# Revit family: ONRIZH
name_source: partatom
category: Mechanical Equipment
units: mm (PartAtom-declared; Revit-internal decimal feet)

## family parameters
Always vertical = Yes
Cut with Voids When Loaded = No
OmniClass Number = 23.40.40.11.17
OmniClass Title = Refrigerated Cases
Part Type = Normal
Room Calculation Point = No
Round Connector Dimension = Use Radius
Shared = No
Work Plane-Based = Yes

## types (5) — shared parameters
22" Shelf = Yes
Certifications = NSF 7, UL471, CSA
DATE = 02/08/2016
DISCHARGE AIR TEMP. = -8 °F
DISCHARGE AIR VELOCITY = 350 FPM
Default Elevation = 48"
Defrost Num Day = 4
Defrost Termination = 50 °F
Defrost Type = ELECTRIC DEFROST
Defrosts Per Day_2 = 1
Description = High Narrow Back-to-Back Reach-In Glass Door Merchandiser
Discharge Air (F) = -1
Discharge Air Velocity (FPM) = 350 FPM
Door Type = Heated
EQUIPMENT DESCRIPTION = High Narrow Back-to-Back Reach-In Glass Door Merchandiser
EQUIPMENT MARK = ONRIZH
Electric Defrost Fail-Safe = 46
Electric Defrost Run-Off Time (Min) = 0
Electric Defrost Termination = 50
Evap Temp = -15
Height = 85 1/4"
Hot Gas Defrost Fail-Safe = 24
Hot Gas Defrost Run-Off Time (Min) = 13-15
Hot Gas Defrost Termination = 73
Item Description = High Narrow Back-to-Back Reach-In Glass Door Merchandiser
Legend Number = ONRIZH
Load Mbh = 1.06
Manufacturer = HILL PHOENIX
Model = ONRIZH
Refrig Charge Lbs = 0
Superheat Set Point @ Bulb (°F) = 3 - 5
URL = http://www.hillphoenix.com
Width = 67 1/8"

## per-type parameters (varying)
- 2- Door Frozen Food: 101-LE DOOR FRAME AMPS=1 A; 101-LE DOOR FRAME WATTS=151 W; 208 Amps SSD Defrost Phase 1=7.5; 208 Watts SSD Defrost Phase 1=1552; 240 Amps SSD Defrost  Phase 1=8.6; 240 Watts SSD Defrost Phase 1=2068; 3 Phase SSD Defrost 208 Amps=6.5; 3 Phase SSD Defrost 208 Watts=1552; 3 Phase SSD Defrost 240 Amps=7.5; 3 Phase SSD Defrost 240 Watts=2068; Application Discipline=Ice Cream; BTUH Conventional=873; BTUH Parallel=848; CENTER LINE & DRAIN=30"; DOOR CONFIGURATION=MASTER DOOR : 30" X 68 3/8" 2 DOOR A SWING (LEFT OPENING); Discharge Air (°F)=-8 °F; Evaporator (°F)=-15 °F; GE Immersion Amps=0.3; Heated Doors Amps=0.78; Heated Doors Watts=67; Heated Option Amps=2.04; Heated Option Watts=219; Length=60"; Low E Doors Amps=0.34; Low E Doors Watts=41; Low E Rails Amps=1.6; Low E Rails Watts=192; SSD Combined Heated Rails Amps=2 A; SSD Combined Heated Rails Watts=219 W; SSD Combined Low E Rails Amps=2 A; SSD Combined Low E Rails Watts=192 W; SSD Fans Per Case=2; SSD High Efficiency Amps=0.6; SSD High Efficiency Fan Watts=50; SSD Individual 101-LE Frame Amps=1 A; SSD Individual 101-LE Frame Watts=151 W; SSD Individual Heated Doors Amps=1 A; SSD Individual Heated Doors Watts=67 W; SSD Individual Low E Doors Amps=0 A; SSD Individual Low E Doors Watts=41 W; SSD Tank Heater Amps=1.3; SSD Tank Heater Watts=152; Size of Doors=Eliminaator/2; Polar LE/EF (Multi-door) Low Energy
- 4-Door Frozen Food: 101-LE DOOR FRAME AMPS=0 A; 101-LE DOOR FRAME WATTS=0 W; 208 Amps SSD Defrost Phase 1=14.3; 208 Watts SSD Defrost Phase 1=1552; 240 Amps SSD Defrost  Phase 1=16.6; 240 Watts SSD Defrost Phase 1=3992; 3 Phase SSD Defrost 208 Amps=12.4; 3 Phase SSD Defrost 208 Watts=2984; 3 Phase SSD Defrost 240 Amps=14.4; 3 Phase SSD Defrost 240 Watts=3992; Application Discipline=Frozen Food; BTUH Conventional=855; BTUH Parallel=831; CENTER LINE & DRAIN=60"; DOOR CONFIGURATION=MASTER DOOR : 30" X 68 3/8" 4 DOOR A SWING (LEFT OPENING); Discharge Air (°F)=-1 °F; Evaporator (°F)=-7 °F; GE Immersion Amps=0.6; Heated Doors Amps=1.56; Heated Doors Watts=135; Heated Option Amps=3.85; Heated Option Watts=410; Length=120"; Low E Doors Amps=0.68; Low E Doors Watts=82; Low E Rails Amps=2.97; Low E Rails Watts=356; SSD Combined Heated Rails Amps=4 A; SSD Combined Heated Rails Watts=410 W; SSD Combined Low E Rails Amps=3 A; SSD Combined Low E Rails Watts=356 W; SSD Fans Per Case=4; SSD High Efficiency Amps=1.3; SSD High Efficiency Fan Watts=100; SSD Individual 101-LE Frame Amps=2 A; SSD Individual 101-LE Frame Watts=275 W; SSD Individual Heated Doors Amps=2 A; SSD Individual Heated Doors Watts=135 W; SSD Individual Low E Doors Amps=1 A; SSD Individual Low E Doors Watts=82 W; SSD Tank Heater Amps=1.9; SSD Tank Heater Watts=226; Size of Doors=Eliminaator/2; Polar LE/EF (Multi-door) Low Energy
- 5-Door Frozen Food: 101-LE DOOR FRAME AMPS=0 A; 101-LE DOOR FRAME WATTS=0 W; 208 Amps SSD Defrost Phase 1=17.5; 208 Watts SSD Defrost Phase 1=3640; 240 Amps SSD Defrost  Phase 1=20.2; 240 Watts SSD Defrost Phase 1=4840; 3 Phase SSD Defrost 208 Amps=15.1; 3 Phase SSD Defrost 208 Watts=3640; 3 Phase SSD Defrost 240 Amps=17.4; 3 Phase SSD Defrost 240 Watts=4840; Application Discipline=Frozen Food; BTUH Conventional=891; BTUH Parallel=866; CENTER LINE & DRAIN=75"; DOOR CONFIGURATION=MASTER DOOR : 30" X 68 3/8" 5 DOOR A SWING (LEFT OPENING); Discharge Air (°F)=-1 °F; Evaporator (°F)=-7 °F; GE Immersion Amps=0.7; Heated Doors Amps=1.56; Heated Doors Watts=135; Heated Option Amps=3.85; Heated Option Watts=410; Length=150"; Low E Doors Amps=0.68; Low E Doors Watts=82; Low E Rails Amps=2.97; Low E Rails Watts=356; SSD Combined Heated Rails Amps=5 A; SSD Combined Heated Rails Watts=502 W; SSD Combined Low E Rails Amps=4 A; SSD Combined Low E Rails Watts=436 W; SSD Fans Per Case=5; SSD High Efficiency Amps=1.6; SSD High Efficiency Fan Watts=125; SSD Individual 101-LE Frame Amps=3 A; SSD Individual 101-LE Frame Watts=334 W; SSD Individual Heated Doors Amps=2 A; SSD Individual Heated Doors Watts=168 W; SSD Individual Low E Doors Amps=1 A; SSD Individual Low E Doors Watts=102 W; SSD Tank Heater Amps=2.3; SSD Tank Heater Watts=275; Size of Doors=ELMD/Polar RE (High)
- 6-Door Frozen Food: 101-LE DOOR FRAME AMPS=0 A; 101-LE DOOR FRAME WATTS=0 W; 208 Amps SSD Defrost Phase 1=20.3; 208 Watts SSD Defrost Phase 1=4224; 240 Amps SSD Defrost  Phase 1=23.4; 240 Watts SSD Defrost Phase 1=5624; 3 Phase SSD Defrost 208 Amps=17.6; 3 Phase SSD Defrost 208 Watts=4224; 3 Phase SSD Defrost 240 Amps=20.3; 3 Phase SSD Defrost 240 Watts=5624; Application Discipline=Ice Cream; BTUH Conventional=928; BTUH Parallel=902; CENTER LINE & DRAIN=90"; DOOR CONFIGURATION=MASTER DOOR : 30" X 68 3/8" 6 DOOR A SWING (LEFT OPENING); Discharge Air (°F)=-8 °F; Evaporator (°F)=-15 °F; GE Immersion Amps=0.8; Heated Doors Amps=2.34; Heated Doors Watts=2; Heated Option Amps=5.62; Heated Option Watts=596; Length=180"; Low E Doors Amps=1.02; Low E Doors Watts=122; Low E Rails Amps=4.3; Low E Rails Watts=516; SSD Combined Heated Rails Amps=6 A; SSD Combined Heated Rails Watts=596 W; SSD Combined Low E Rails Amps=4 A; SSD Combined Low E Rails Watts=516 W; SSD Fans Per Case=6; SSD High Efficiency Amps=1.9; SSD High Efficiency Fan Watts=150; SSD Individual 101-LE Frame Amps=3 A; SSD Individual 101-LE Frame Watts=394 W; SSD Individual Heated Doors Amps=2 A; SSD Individual Heated Doors Watts=202 W; SSD Individual Low E Doors Amps=1 A; SSD Individual Low E Doors Watts=122 W; SSD Tank Heater Amps=2.7; SSD Tank Heater Watts=320
- 3- Door Frozen Food: 101-LE DOOR FRAME AMPS=1 A; 101-LE DOOR FRAME WATTS=151 W; 208 Amps SSD Defrost Phase 1=7.5; 208 Watts SSD Defrost Phase 1=1552; 240 Amps SSD Defrost  Phase 1=8.6; 240 Watts SSD Defrost Phase 1=2068; 3 Phase SSD Defrost 208 Amps=6.5; 3 Phase SSD Defrost 208 Watts=1552; 3 Phase SSD Defrost 240 Amps=7.5; 3 Phase SSD Defrost 240 Watts=2068; Application Discipline=Ice Cream; BTUH Conventional=873; BTUH Parallel=848; CENTER LINE & DRAIN=45"; DOOR CONFIGURATION=MASTER DOOR : 30" X 68 3/8" 3 DOOR A SWING (LEFT OPENING); Discharge Air (°F)=-8 °F; Evaporator (°F)=-15 °F; GE Immersion Amps=0.3; Heated Doors Amps=0.78; Heated Doors Watts=67; Heated Option Amps=2.04; Heated Option Watts=219; Length=90"; Low E Doors Amps=0.34; Low E Doors Watts=41; Low E Rails Amps=1.6; Low E Rails Watts=192; SSD Combined Heated Rails Amps=2 A; SSD Combined Heated Rails Watts=219 W; SSD Combined Low E Rails Amps=2 A; SSD Combined Low E Rails Watts=192 W; SSD Fans Per Case=2; SSD High Efficiency Amps=0.6; SSD High Efficiency Fan Watts=50; SSD Individual 101-LE Frame Amps=1 A; SSD Individual 101-LE Frame Watts=151 W; SSD Individual Heated Doors Amps=1 A; SSD Individual Heated Doors Watts=67 W; SSD Individual Low E Doors Amps=0 A; SSD Individual Low E Doors Watts=41 W; SSD Tank Heater Amps=1.3; SSD Tank Heater Watts=152; Size of Doors=Eliminaator/2; Polar LE/EF (Multi-door) Low Energy

## geometry (parser evidence)
native form markers: Blend x8, Sweep x14
no freeform markers — native parametric forms only
